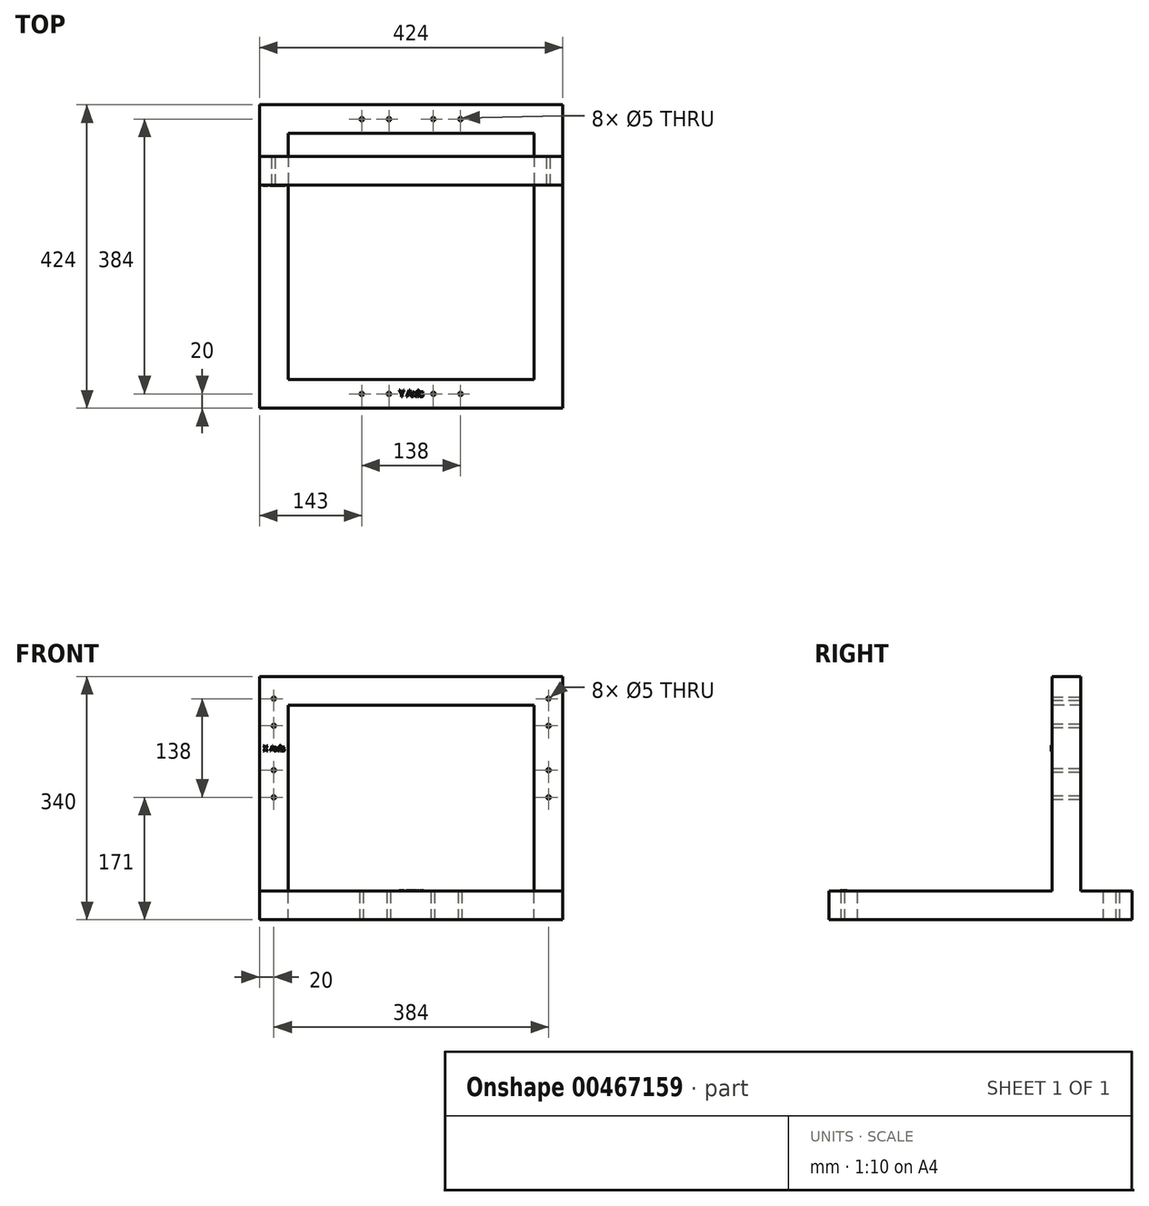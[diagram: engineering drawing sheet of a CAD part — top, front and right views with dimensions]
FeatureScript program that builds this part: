
annotation { "Feature Type Name" : "Feature", "Feature Type Description" : "" }
export const myFeature = defineFeature(function(context is Context, id is Id, definition is map)
    precondition{}
    {
        {
            assignVariable(context, id + "F0", {"name" : "Stand_height", "anyValue" : 300 * mm});
        }
        {
            assignVariable(context, id + "F1", {"name" : "Stand_inner", "anyValue" : 400 - 2 * 8 - 2 * 20});
        }
        {
            var Q0;
            Q0=qCreatedBy(makeId("Top.planeOp"),FACE);
            var sketch = newSketch(context, id + "F2", { "sketchPlane" : qUnion([Q0])});
            skLineSegment(sketch, "E0.bottom", {"start": v(-172, 172) * mm, "end": v(172, 172) * mm});
            skLineSegment(sketch, "E0.top", {"start": v(-172, -172) * mm, "end": v(172, -172) * mm});
            skLineSegment(sketch, "E0.left", {"start": v(-172, 172) * mm, "end": v(-172, -172) * mm});
            skLineSegment(sketch, "E0.right", {"start": v(172, 172) * mm, "end": v(172, -172) * mm});
            skPoint(sketch, "E0.middle", {"position": v(0, 0) * mm});
            skLineSegment(sketch, "E1.bottom", {"start": v(-212, 212) * mm, "end": v(212, 212) * mm});
            skLineSegment(sketch, "E1.top", {"start": v(-212, -212) * mm, "end": v(212, -212) * mm});
            skLineSegment(sketch, "E1.left", {"start": v(-212, 212) * mm, "end": v(-212, -212) * mm});
            skLineSegment(sketch, "E1.right", {"start": v(212, 212) * mm, "end": v(212, -212) * mm});
            skPoint(sketch, "E2", {"position": v(-69, -192) * mm});
            skPoint(sketch, "E3", {"position": v(-31, -192) * mm});
            skPoint(sketch, "E4", {"position": v(-50, -192) * mm});
            skPoint(sketch, "E5.0.1.0", {"position": v(-31, 192) * mm});
            skPoint(sketch, "E5.0.1.1", {"position": v(-50, 192) * mm});
            skPoint(sketch, "E5.0.1.2", {"position": v(-69, 192) * mm});
            skPoint(sketch, "E5.0.1.3", {"position": v(-69, 192) * mm});
            skPoint(sketch, "E5.1.0.0", {"position": v(69, -192) * mm});
            skPoint(sketch, "E5.1.0.1", {"position": v(50, -192) * mm});
            skPoint(sketch, "E5.1.0.2", {"position": v(31, -192) * mm});
            skPoint(sketch, "E5.1.0.3", {"position": v(31, -192) * mm});
            skPoint(sketch, "E5.1.1.0", {"position": v(69, 192) * mm});
            skPoint(sketch, "E5.1.1.1", {"position": v(50, 192) * mm});
            skPoint(sketch, "E5.1.1.2", {"position": v(31, 192) * mm});
            skPoint(sketch, "E5.1.1.3", {"position": v(31, 192) * mm});
            skLineSegment(sketch, "E5.direction1", {"start": v(-69, -192) * mm, "end": v(31, -192) * mm, "construction": true});
            skLineSegment(sketch, "E5.direction2", {"start": v(-69, -192) * mm, "end": v(-69, 192) * mm, "construction": true});
            skSolve(sketch);
        }
        {
            var Q0;
            Q0=makeQuery(id+"F2.imprint","IMPRINT",FACE,{"disambiguationData":[TD([[makeQuery(id+"F2.imprint","IMPRINT",EDGE,{"derivedFrom":sQuery(id+"F2.wireOp",EDGE,"E0.bottom")}),1.0]])]});
            extrude(context, id + "F3", {"entities" : qUnion([Q0]), "oppositeDirection" : true, "depth" : 40 * mm});
        }
        {
            var Q0;
            Q0=qCreatedBy(makeId("Right.planeOp"),FACE);
            var sketch = newSketch(context, id + "F4", { "sketchPlane" : qUnion([Q0])});
            skLineSegment(sketch, "E6.bottom", {"start": v(100, 0) * mm, "end": v(140, 0) * mm});
            skLineSegment(sketch, "E6.top", {"start": v(100, 300) * mm, "end": v(140, 300) * mm});
            skLineSegment(sketch, "E6.left", {"start": v(100, 0) * mm, "end": v(100, 300) * mm});
            skLineSegment(sketch, "E6.right", {"start": v(140, 0) * mm, "end": v(140, 300) * mm});
            skSolve(sketch);
        }
        {
            var Q0;
            Q0 = qSketchRegion(id + "F4", true);
            extrude(context, id + "F5", {"entities" : qUnion([Q0]), "depth" : 40 * mm});
        }
        {
            var Q0;
            Q0=makeQuery(id+"F5.opExtrude","SWEPT_BODY",BODY,{"disambiguationData":[OSD([sQuery(id+"F4.wireOp",EDGE,"E6.bottom"),sQuery(id+"F4.wireOp",EDGE,"E6.top"),sQuery(id+"F4.wireOp",EDGE,"E6.left"),sQuery(id+"F4.wireOp",EDGE,"E6.right")])]});
            var Q1;
            Q1=qCreatedBy(makeId("Right.planeOp"),FACE);
            transform(context, id + "F6", {"entities" : qUnion([Q0]), "transformType" : TransformType.TRANSLATION_DISTANCE, "transformDirection" : qUnion([Q1]), "distance" : (getVariable(context, 'Stand_inner') / 2) * mm, "makeCopy" : false});
        }
        {
            var Q0;
            Q0=makeQuery(id+"F5.opExtrude","SWEPT_BODY",BODY,{"disambiguationData":[OSD([sQuery(id+"F4.wireOp",EDGE,"E6.bottom"),sQuery(id+"F4.wireOp",EDGE,"E6.top"),sQuery(id+"F4.wireOp",EDGE,"E6.left"),sQuery(id+"F4.wireOp",EDGE,"E6.right")])]});
            var Q1;
            Q1=qCreatedBy(makeId("Right.planeOp"),FACE);
            mirror(context, id + "F7", {"operationType" : NewBodyOperationType.ADD, "entities" : qUnion([Q0]), "mirrorPlane" : qUnion([Q1])});
        }
        {
            var Q0;
            Q0=qCreatedBy(makeId("Top.planeOp"),FACE);
            cPlane(context, id + "F8", {"entities" : qUnion([Q0]), "cplaneType" : CPlaneType.OFFSET, "offset" : getVariable(context, 'Stand_height'), "width" : 152.4 * mm, "height" : 152.4 * mm});
        }
        {
            var Q0;
            Q0=qCreatedBy(id+"F8.planeOp",FACE);
            var sketch = newSketch(context, id + "F9", { "sketchPlane" : qUnion([Q0])});
            skLineSegment(sketch, "E7.bottom", {"start": v(-172, 140) * mm, "end": v(172, 140) * mm});
            skLineSegment(sketch, "E7.top", {"start": v(-172, 100) * mm, "end": v(172, 100) * mm});
            skLineSegment(sketch, "E7.left", {"start": v(-172, 140) * mm, "end": v(-172, 100) * mm});
            skLineSegment(sketch, "E7.right", {"start": v(172, 140) * mm, "end": v(172, 100) * mm});
            skSolve(sketch);
        }
        {
            var Q0;
            Q0=makeQuery(id+"F9.imprint","IMPRINT",FACE,{"disambiguationData":[TD([[makeQuery(id+"F9.imprint","IMPRINT",EDGE,{"derivedFrom":sQuery(id+"F9.wireOp",EDGE,"E7.bottom")}),-1.0]])]});
            extrude(context, id + "F10", {"entities" : qUnion([Q0]), "operationType" : NewBodyOperationType.ADD, "oppositeDirection" : true, "depth" : 40 * mm});
        }
        {
            var Q0;
            {var subQ0=makeQuery(id+"F5.opExtrude","SWEPT_FACE",FACE,{"disambiguationData":[OSD([sQuery(id+"F4.wireOp",EDGE,"E6.right")])]});Q0=makeQuery(id+"F10.boolean.opBoolean","MERGE",FACE,{"derivedFrom":[subQ0,makeQuery(id+"F7.opPattern","COPY",FACE,{"derivedFrom":subQ0,"instanceName":"1"}),makeQuery(id+"F10.opExtrude","SWEPT_FACE",FACE,{"disambiguationData":[OSD([sQuery(id+"F9.wireOp",EDGE,"E7.bottom")])]})]});}
            var sketch = newSketch(context, id + "F11", { "sketchPlane" : qUnion([Q0])});
            skPoint(sketch, "E8", {"position": v(-192, 269) * mm});
            skPoint(sketch, "E9", {"position": v(-192, 250) * mm});
            skPoint(sketch, "E10", {"position": v(-192, 231) * mm});
            skPoint(sketch, "E11.0.1.0", {"position": v(-192, 131) * mm});
            skPoint(sketch, "E11.0.1.1", {"position": v(-192, 150) * mm});
            skPoint(sketch, "E11.0.1.2", {"position": v(-192, 169) * mm});
            skPoint(sketch, "E11.1.0.0", {"position": v(192, 231) * mm});
            skPoint(sketch, "E11.1.0.1", {"position": v(192, 250) * mm});
            skPoint(sketch, "E11.1.0.2", {"position": v(192, 269) * mm});
            skPoint(sketch, "E11.1.1.0", {"position": v(192, 131) * mm});
            skPoint(sketch, "E11.1.1.1", {"position": v(192, 150) * mm});
            skPoint(sketch, "E11.1.1.2", {"position": v(192, 169) * mm});
            skLineSegment(sketch, "E11.direction1", {"start": v(-192, 231) * mm, "end": v(192, 231) * mm, "construction": true});
            skLineSegment(sketch, "E11.direction2", {"start": v(-192, 231) * mm, "end": v(-192, 131) * mm, "construction": true});
            skSolve(sketch);
        }
        {
            var Q0;
            Q0=sQuery(id+"F2.wireOp",VERTEX,"E2");
            var Q1;
            Q1=sQuery(id+"F2.wireOp",VERTEX,"E3");
            var Q2;
            Q2=sQuery(id+"F2.wireOp",VERTEX,"E5.1.0.2");
            var Q3;
            Q3=sQuery(id+"F2.wireOp",VERTEX,"E5.1.0.0");
            var Q4;
            Q4=sQuery(id+"F2.wireOp",VERTEX,"E5.0.1.2");
            var Q5;
            Q5=sQuery(id+"F2.wireOp",VERTEX,"E5.0.1.0");
            var Q6;
            Q6=sQuery(id+"F2.wireOp",VERTEX,"E5.1.1.2");
            var Q7;
            Q7=sQuery(id+"F2.wireOp",VERTEX,"E5.1.1.0");
            var Q8;
            Q8=sQuery(id+"F11.wireOp",VERTEX,"E8");
            var Q9;
            Q9=sQuery(id+"F11.wireOp",VERTEX,"E10");
            var Q10;
            Q10=sQuery(id+"F11.wireOp",VERTEX,"E11.0.1.2");
            var Q11;
            Q11=sQuery(id+"F11.wireOp",VERTEX,"E11.0.1.0");
            var Q12;
            Q12=sQuery(id+"F11.wireOp",VERTEX,"E11.1.0.2");
            var Q13;
            Q13=sQuery(id+"F11.wireOp",VERTEX,"E11.1.0.0");
            var Q14;
            Q14=sQuery(id+"F11.wireOp",VERTEX,"E11.1.1.2");
            var Q15;
            Q15=sQuery(id+"F11.wireOp",VERTEX,"E11.1.1.0");
            var Q16;
            Q16=makeQuery(id+"F3.opExtrude","SWEPT_BODY",BODY,{"disambiguationData":[OSD([sQuery(id+"F2.wireOp",EDGE,"E0.bottom"),sQuery(id+"F2.wireOp",EDGE,"E0.top"),sQuery(id+"F2.wireOp",EDGE,"E0.left"),sQuery(id+"F2.wireOp",EDGE,"E0.right"),sQuery(id+"F2.wireOp",EDGE,"E1.bottom"),sQuery(id+"F2.wireOp",EDGE,"E1.top"),sQuery(id+"F2.wireOp",EDGE,"E1.left"),sQuery(id+"F2.wireOp",EDGE,"E1.right")])]});
            hole(context, id + "F12", {"style" : HoleStyle.SIMPLE, "endStyle" : HoleEndStyle.THROUGH, "holeDiameter" : 5 * mm, "isTappedThrough" : true, "tappedDepth" : 12 * mm, "tapClearance" : 3, "locations" : qUnion([Q0, Q1, Q2, Q3, Q4, Q5, Q6, Q7, Q8, Q9, Q10, Q11, Q12, Q13, Q14, Q15]), "scope" : qUnion([Q16])});
        }
        {
            var Q0;
            {var subQ0=makeQuery(id+"F5.opExtrude","SWEPT_FACE",FACE,{"disambiguationData":[OSD([sQuery(id+"F4.wireOp",EDGE,"E6.left")])]});Q0=makeQuery(id+"F10.boolean.opBoolean","MERGE",FACE,{"derivedFrom":[subQ0,makeQuery(id+"F7.opPattern","COPY",FACE,{"derivedFrom":subQ0,"instanceName":"1"}),makeQuery(id+"F10.opExtrude","SWEPT_FACE",FACE,{"disambiguationData":[OSD([sQuery(id+"F9.wireOp",EDGE,"E7.top")])]})]});}
            var sketch = newSketch(context, id + "F13", { "sketchPlane" : qUnion([Q0])});
            skText(sketch, "E12", { "text": "X Axis\n", "fontName": "OpenSans-Regular.ttf"});
            const initialGuessF13  = {"E12": [-0.20674, 0.19548, 1, 0, 0.00804]};
            skSetInitialGuess(sketch, initialGuessF13);
            skSolve(sketch);
        }
        {
            var Q0;
            {var subQ5=sQuery(id+"F2.wireOp",EDGE,"E0.right");var subQ6=sQuery(id+"F2.wireOp",EDGE,"E1.right");var subQ7=sQuery(id+"F2.wireOp",EDGE,"E1.left");var subQ10=sQuery(id+"F2.wireOp",EDGE,"E0.top");var subQ11=sQuery(id+"F2.wireOp",EDGE,"E0.left");var subQ12=sQuery(id+"F2.wireOp",EDGE,"E1.top");Q0=makeQuery(id+"F7.boolean.opBoolean","SPLIT",FACE,{"disambiguationData":[TD([makeQuery(id+"F3.opExtrude","SWEPT_FACE",FACE,{"disambiguationData":[OSD([subQ10])]})])],"derivedFrom":makeQuery(id+"F3.opExtrude","CAP_FACE",FACE,{"disambiguationData":[OSD([sQuery(id+"F2.wireOp",EDGE,"E0.bottom"),subQ10,subQ11,subQ5,sQuery(id+"F2.wireOp",EDGE,"E1.bottom"),subQ12,subQ7,subQ6])],"isStart":true})});}
            var sketch = newSketch(context, id + "F14", { "sketchPlane" : qUnion([Q0])});
            skText(sketch, "E13", { "text": "Y Axis", "fontName": "OpenSans-Regular.ttf"});
            const initialGuessF14  = {"E13": [-0.01672, -0.19582, 1, 0, 0.0091]};
            skSetInitialGuess(sketch, initialGuessF14);
            skSolve(sketch);
        }
        {
            var Q0;
            Q0 = qSketchRegion(id + "F14", true);
            extrude(context, id + "F15", {"entities" : qUnion([Q0]), "operationType" : NewBodyOperationType.ADD, "depth" : 1 * mm});
        }
        {
            var Q0;
            Q0 = qSketchRegion(id + "F13", true);
            extrude(context, id + "F16", {"entities" : qUnion([Q0]), "operationType" : NewBodyOperationType.ADD, "depth" : 1 * mm});
        }
    });
